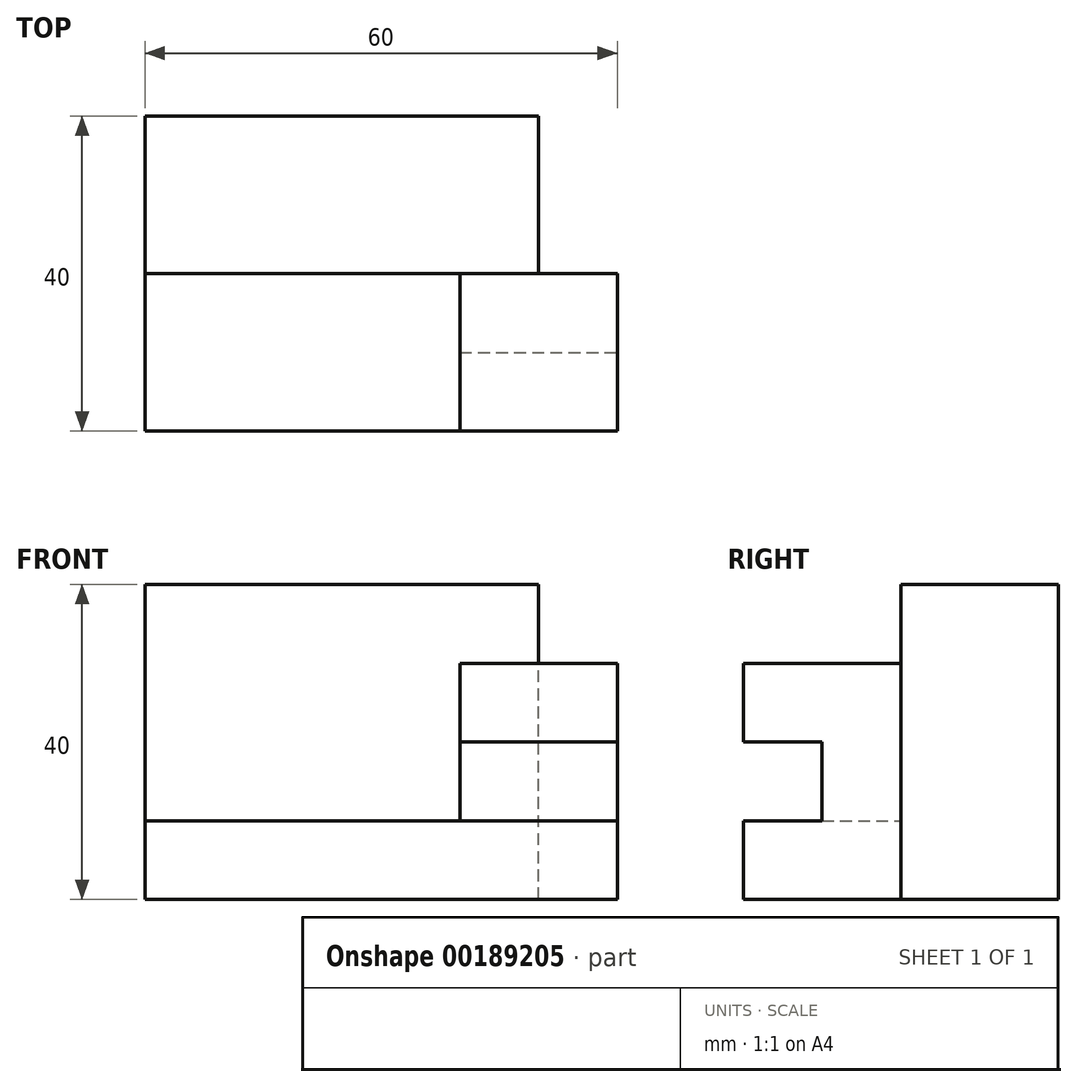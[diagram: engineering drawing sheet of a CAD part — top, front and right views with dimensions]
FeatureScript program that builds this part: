
annotation { "Feature Type Name" : "Feature", "Feature Type Description" : "" }
export const myFeature = defineFeature(function(context is Context, id is Id, definition is map)
    precondition{}
    {
        {
            var Q0;
            Q0=qCreatedBy(makeId("Front.planeOp"),FACE);
            var sketch = newSketch(context, id + "F0", { "sketchPlane" : qUnion([Q0])});
            skLineSegment(sketch, "E0.bottom", {"start": v(0, 0) * mm, "end": v(50, 0) * mm});
            skLineSegment(sketch, "E0.top", {"start": v(0, 40) * mm, "end": v(50, 40) * mm});
            skLineSegment(sketch, "E0.left", {"start": v(0, 0) * mm, "end": v(0, 40) * mm});
            skLineSegment(sketch, "E0.right", {"start": v(50, 0) * mm, "end": v(50, 40) * mm});
            skSolve(sketch);
        }
        {
            var Q0;
            Q0=makeQuery(id+"F0.imprint","IMPRINT",FACE,{"disambiguationData":[TD([[makeQuery(id+"F0.imprint","IMPRINT",EDGE,{"derivedFrom":sQuery(id+"F0.wireOp",EDGE,"E0.bottom")}),1.0]])]});
            extrude(context, id + "F1", {"entities" : qUnion([Q0]), "depth" : 20 * mm});
        }
        {
            var Q0;
            Q0=makeQuery(id+"F1.opExtrude","CAP_FACE",FACE,{"disambiguationData":[OSD([sQuery(id+"F0.wireOp",EDGE,"E0.bottom"),sQuery(id+"F0.wireOp",EDGE,"E0.top"),sQuery(id+"F0.wireOp",EDGE,"E0.left"),sQuery(id+"F0.wireOp",EDGE,"E0.right")])],"isStart":false});
            var sketch = newSketch(context, id + "F2", { "sketchPlane" : qUnion([Q0])});
            skLineSegment(sketch, "E1.bottom", {"start": v(0, 0) * mm, "end": v(60, 0) * mm});
            skLineSegment(sketch, "E1.top", {"start": v(0, 10) * mm, "end": v(60, 10) * mm});
            skLineSegment(sketch, "E1.left", {"start": v(0, 0) * mm, "end": v(0, 10) * mm});
            skLineSegment(sketch, "E1.right", {"start": v(60, 0) * mm, "end": v(60, 10) * mm});
            skSolve(sketch);
        }
        {
            var Q0;
            {var subQ0=sQuery(id+"F2.wireOp",EDGE,"E1.left");Q0=makeQuery(id+"F2.imprint","IMPRINT",FACE,{"disambiguationData":[TD([[makeQuery(id+"F2.imprint","IMPRINT",EDGE,{"derivedFrom":subQ0}),-1.0]])]});}
            var Q1;
            {var subQ3=sQuery(id+"F2.wireOp",EDGE,"E1.right");Q1=makeQuery(id+"F2.imprint","IMPRINT",FACE,{"disambiguationData":[TD([[makeQuery(id+"F2.imprint","IMPRINT",EDGE,{"derivedFrom":subQ3}),1.0]])]});}
            extrude(context, id + "F3", {"entities" : qUnion([Q0, Q1]), "operationType" : NewBodyOperationType.ADD, "depth" : 20 * mm});
        }
        {
            var Q0;
            Q0=makeQuery(id+"F3.opExtrude","SWEPT_FACE",FACE,{"disambiguationData":[OSD([sQuery(id+"F2.wireOp",EDGE,"E1.right")])]});
            var sketch = newSketch(context, id + "F4", { "sketchPlane" : qUnion([Q0])});
            skLineSegment(sketch, "E2", {"start": v(-30, 10) * mm, "end": v(-30, 20) * mm});
            skLineSegment(sketch, "E3", {"start": v(-30, 20) * mm, "end": v(-40, 20) * mm});
            skLineSegment(sketch, "E4", {"start": v(-40, 20) * mm, "end": v(-40, 30) * mm});
            skLineSegment(sketch, "E5", {"start": v(-40, 30) * mm, "end": v(-20, 30) * mm});
            skLineSegment(sketch, "E6", {"start": v(-20, 30) * mm, "end": v(-20, 10) * mm});
            skLineSegment(sketch, "E7.0", {"start": v(-30, 10) * mm, "end": v(-20, 10) * mm});
            skPoint(sketch, "E8.orphan", {"position": v(-40, 10) * mm});
            skSolve(sketch);
        }
        {
            var Q0;
            Q0=makeQuery(id+"F4.imprint","IMPRINT",FACE,{"disambiguationData":[TD([[makeQuery(id+"F4.imprint","IMPRINT",EDGE,{"derivedFrom":sQuery(id+"F4.wireOp",EDGE,"E2")}),-1.0]])]});
            extrude(context, id + "F5", {"entities" : qUnion([Q0]), "operationType" : NewBodyOperationType.ADD, "oppositeDirection" : true, "depth" : 20 * mm});
        }
    });
